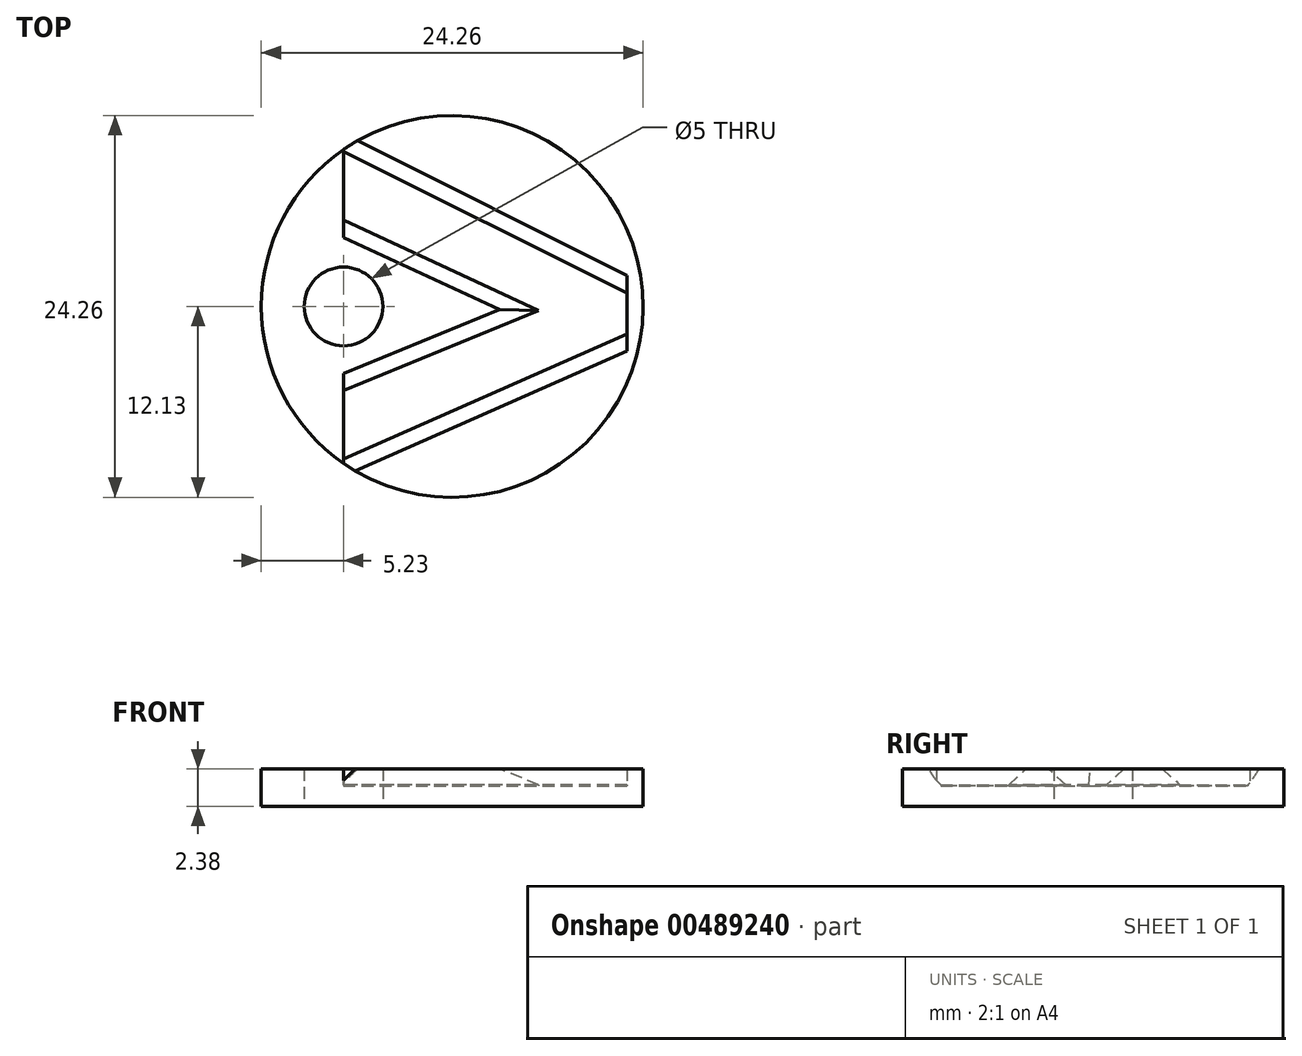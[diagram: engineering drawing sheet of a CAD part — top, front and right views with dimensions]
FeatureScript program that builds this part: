
annotation { "Feature Type Name" : "Feature", "Feature Type Description" : "" }
export const myFeature = defineFeature(function(context is Context, id is Id, definition is map)
    precondition{}
    {
        {
            var Q0;
            Q0=qCreatedBy(makeId("Top.planeOp"),FACE);
            var sketch = newSketch(context, id + "F0", { "sketchPlane" : qUnion([Q0])});
            skCircle(sketch, "E0", {"center": v(0, 0) * mm, "radius": 12.13 * mm});
            skText(sketch, "E1", { "text": ">", "fontName": "OpenSans-Bold.ttf"});
            skCircle(sketch, "E2", {"center": v(-6.9, 0) * mm, "radius": 2.5 * mm});
            const initialGuessF0  = {"E1": [-0.0085, -0.01336, 1, 0, 0.02673]};
            skSetInitialGuess(sketch, initialGuessF0);
            skSolve(sketch);
        }
        {
            var Q0;
            Q0 = qSketchRegion(id + "F0", true);
            extrude(context, id + "F1", {"entities" : qUnion([Q0]), "depth" : 2.38 * mm});
        }
        {
            var Q0;
            Q0=qCreatedBy(makeId("Top.planeOp"),FACE);
            var sketch = newSketch(context, id + "F2", { "sketchPlane" : qUnion([Q0])});
            skCircle(sketch, "E3", {"center": v(0, 0) * mm, "radius": 12.12 * mm});
            skSolve(sketch);
        }
        {
            var Q0;
            Q0 = qSketchRegion(id + "F2", true);
            extrude(context, id + "F3", {"entities" : qUnion([Q0]), "operationType" : NewBodyOperationType.ADD, "depth" : 1.3 * mm});
        }
        {
            var Q0;
            Q0=makeQuery(id+"F1.opExtrude","CAP_EDGE",EDGE,{"disambiguationData":[OSD([sQuery(id+"F0.wireOp",EDGE,"E1.sketch_text.stroke-3")])],"isStart":false});
            var Q1;
            Q1=makeQuery(id+"F1.opExtrude","CAP_EDGE",EDGE,{"disambiguationData":[OSD([sQuery(id+"F0.wireOp",EDGE,"E1.sketch_text.stroke-1")])],"isStart":false});
            var Q2;
            Q2=makeQuery(id+"F1.opExtrude","CAP_EDGE",EDGE,{"disambiguationData":[OSD([sQuery(id+"F0.wireOp",EDGE,"E1.sketch_text.stroke-0")])],"isStart":false});
            var Q3;
            Q3=makeQuery(id+"F1.opExtrude","CAP_EDGE",EDGE,{"disambiguationData":[OSD([sQuery(id+"F0.wireOp",EDGE,"E1.sketch_text.stroke-5")])],"isStart":false});
            chamfer(context, id + "F4", {"entities" : qUnion([Q0, Q1, Q2, Q3]), "width" : 1 * mm, "tangentPropagation" : true});
        }
        {
            var Q0;
            Q0=makeQuery(id+"F4.opChamfer","SPLIT",FACE,{"disambiguationData":[OD(0.0)],"derivedFrom":makeQuery(id+"F1.opExtrude","CAP_FACE",FACE,{"disambiguationData":[OSD([sQuery(id+"F0.wireOp",EDGE,"E0"),sQuery(id+"F0.wireOp",EDGE,"E1.sketch_text.stroke-0"),sQuery(id+"F0.wireOp",EDGE,"E1.sketch_text.stroke-1"),sQuery(id+"F0.wireOp",EDGE,"E1.sketch_text.stroke-2"),sQuery(id+"F0.wireOp",EDGE,"E1.sketch_text.stroke-3"),sQuery(id+"F0.wireOp",EDGE,"E1.sketch_text.stroke-4"),sQuery(id+"F0.wireOp",EDGE,"E1.sketch_text.stroke-5"),sQuery(id+"F0.wireOp",EDGE,"E1.sketch_text.stroke-6"),sQuery(id+"F0.wireOp",EDGE,"E2")])],"isStart":false})});
            var sketch = newSketch(context, id + "F5", { "sketchPlane" : qUnion([Q0])});
            skCircle(sketch, "E4", {"center": v(-6.9, 0) * mm, "radius": 2.5 * mm});
            skSolve(sketch);
        }
        {
            var Q0;
            Q0 = qSketchRegion(id + "F5", true);
            extrude(context, id + "F6", {"entities" : qUnion([Q0]), "operationType" : NewBodyOperationType.REMOVE, "oppositeDirection" : true, "depth" : 25 * mm});
        }
    });
